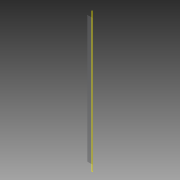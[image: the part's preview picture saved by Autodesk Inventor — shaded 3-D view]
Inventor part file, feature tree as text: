
AUTODESK INVENTOR PART (.ipt)
format: ipt  version: 2013 (Build 170138000, 138)  size: 67,584 bytes
history: native  units: in
note: dims shown in document units (in); Inventor stores cm internally (conversion verified against a paired STEP export)
features: plane x1, extrude x1, sketch x1, reference x1
ambient origin geometry x8: Origin, YZ Plane, XZ Plane, XY Plane, X Axis, Y Axis, Z Axis, Center Point
bodies: Solid1 (feature_tree)
feature tree (4):
  plane  "Work Plane1"
  extrude  "Extrusion1"  [1 undecoded]
  sketch  "Sketch1"  dims[d0=0.25in d1=0.0in]
  reference  "Reference1"
note: 1 required parameter value undecoded (feature->parameter linkage not recoverable at this tier; creation-order binding heuristic only, values carry confidence <= 0.55)
